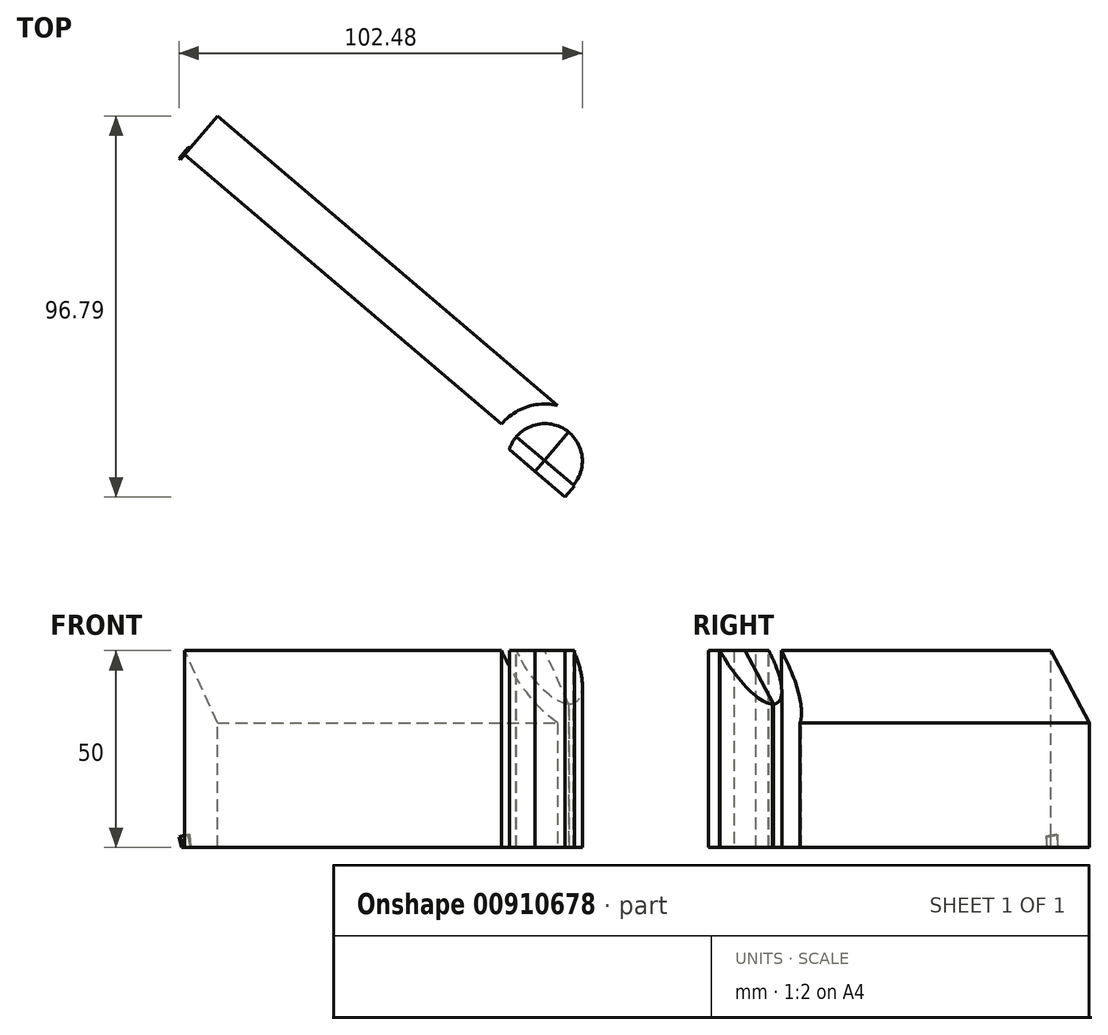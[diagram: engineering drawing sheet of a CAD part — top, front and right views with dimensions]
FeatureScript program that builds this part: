
annotation { "Feature Type Name" : "Feature", "Feature Type Description" : "" }
export const myFeature = defineFeature(function(context is Context, id is Id, definition is map)
    precondition{}
    {
        {
            var Q0;
            Q0=qCreatedBy(makeId("Top.planeOp"),FACE);
            var sketch = newSketch(context, id + "F0", { "sketchPlane" : qUnion([Q0])});
            skArc(sketch, "E0", {"start": v(-9.5, 0) * mm, "mid": v(4.39, 8.43) * mm, "end": v(5.45, -7.78) * mm});
            skLineSegment(sketch, "E1", {"start": v(0, 0) * mm, "end": v(-9.5, 0) * mm, "construction": true});
            skLineSegment(sketch, "E2", {"start": v(0, 0) * mm, "end": v(5.45, -7.78) * mm, "construction": true});
            skArc(sketch, "E3", {"start": v(-14.5, 0) * mm, "mid": v(6.7, 12.86) * mm, "end": v(8.32, -11.88) * mm});
            skLineSegment(sketch, "E4", {"start": v(-14.5, 0) * mm, "end": v(-9.5, 0) * mm});
            skLineSegment(sketch, "E5", {"start": v(5.45, -7.78) * mm, "end": v(8.32, -11.88) * mm});
            skCircle(sketch, "E6", {"center": v(0, 0) * mm, "radius": 9.5 * mm, "construction": true});
            skCircle(sketch, "E7", {"center": v(0, 0) * mm, "radius": 14.5 * mm, "construction": true});
            skSolve(sketch);
        }
        {
            var Q0;
            Q0 = qSketchRegion(id + "F0", true);
            extrude(context, id + "F1", {"entities" : qUnion([Q0]), "depth" : 50 * mm, "offsetDistance" : 25.4 * mm});
        }
        {
            var Q0;
            Q0=makeQuery(id+"F1.opExtrude","CAP_FACE",FACE,{"disambiguationData":[OSD([sQuery(id+"F0.wireOp",EDGE,"E0"),sQuery(id+"F0.wireOp",EDGE,"E3"),sQuery(id+"F0.wireOp",EDGE,"E4"),sQuery(id+"F0.wireOp",EDGE,"E5")])],"isStart":true});
            var sketch = newSketch(context, id + "F2", { "sketchPlane" : qUnion([Q0])});
            skLineSegment(sketch, "E8", {"start": v(-6.15, 7.24) * mm, "end": v(0, 0) * mm, "construction": true});
            skSolve(sketch);
        }
        {
            var Q0;
            Q0=sQuery(id+"F2.wireOp",EDGE,"E8");
            cPlane(context, id + "F3", {"entities" : qUnion([Q0]), "cplaneType" : CPlaneType.LINE_ANGLE, "offset" : 25.4 * mm, "angle" : 90 * degree, "width" : 152.4 * mm, "height" : 152.4 * mm});
        }
        {
            var Q0;
            Q0=qCreatedBy(id+"F3.planeOp",FACE);
            cPlane(context, id + "F4", {"entities" : qUnion([Q0]), "cplaneType" : CPlaneType.OFFSET, "offset" : 2.9 / 20 * mm, "width" : 152.4 * mm, "height" : 152.4 * mm});
        }
        {
            var Q0;
            Q0=makeQuery(id+"F1.opExtrude","SWEPT_EDGE",EDGE,{"disambiguationData":[OSD([sQuery(id+"F0.wireOp",EDGE,"E0"),sQuery(id+"F0.wireOp",EDGE,"E5")])]});
            var Q1;
            Q1=makeQuery(id+"F1.opExtrude","SWEPT_EDGE",EDGE,{"disambiguationData":[OSD([sQuery(id+"F0.wireOp",EDGE,"E0"),sQuery(id+"F0.wireOp",EDGE,"E4")])]});
            fillet(context, id + "F5", {"entities" : qUnion([Q0, Q1]), "radius" : 5 * mm, "tangentPropagation" : true, "allowEdgeOverflow" : false});
        }
        {
            var Q0;
            Q0=qCreatedBy(id+"F4.planeOp",FACE);
            var sketch = newSketch(context, id + "F6", { "sketchPlane" : qUnion([Q0])});
            skLineSegment(sketch, "E9", {"start": v(0, 0) * mm, "end": v(0, 50) * mm, "construction": true});
            skLineSegment(sketch, "E10", {"start": v(35.01, 0) * mm, "end": v(0, 0) * mm, "construction": true});
            skLineSegment(sketch, "E11", {"start": v(35.01, 0) * mm, "end": v(25.18, -6.88) * mm, "construction": true});
            skLineSegment(sketch, "E12", {"start": v(0, 50) * mm, "end": v(-9.83, 43.12) * mm, "construction": true});
            skLineSegment(sketch, "E13", {"start": v(-9.83, 43.12) * mm, "end": v(25.18, -6.88) * mm, "construction": true});
            skLineSegment(sketch, "E14", {"start": v(0, 50) * mm, "end": v(-3.66, 50) * mm, "construction": true});
            skLineSegment(sketch, "E15", {"start": v(-3.66, 50) * mm, "end": v(-3.66, 47.44) * mm, "construction": true});
            skLineSegment(sketch, "E16", {"start": v(-3.66, 47.44) * mm, "end": v(-3.66, 34.3) * mm, "construction": true});
            skLineSegment(sketch, "E17", {"start": v(-3.66, 50) * mm, "end": v(12.84, 50) * mm, "construction": true});
            skLineSegment(sketch, "E18", {"start": v(12.84, 50) * mm, "end": v(12.84, 0) * mm, "construction": true});
            skLineSegment(sketch, "E19", {"start": v(0, 50) * mm, "end": v(-3.66, 50) * mm});
            skLineSegment(sketch, "E20", {"start": v(-3.66, 50) * mm, "end": v(-3.66, 34.3) * mm});
            skLineSegment(sketch, "E21", {"start": v(-3.66, 34.3) * mm, "end": v(12.84, 10.74) * mm});
            skLineSegment(sketch, "E22", {"start": v(12.84, 10.74) * mm, "end": v(12.84, 0) * mm});
            skLineSegment(sketch, "E23", {"start": v(-3.66, 0) * mm, "end": v(12.84, 0) * mm});
            skLineSegment(sketch, "E24", {"start": v(12.84, 10.74) * mm, "end": v(12.84, 31.66) * mm});
            skLineSegment(sketch, "E25", {"start": v(12.84, 31.66) * mm, "end": v(0, 50) * mm});
            skLineSegment(sketch, "E26", {"start": v(0, 50) * mm, "end": v(35.01, 0) * mm, "construction": true});
            skLineSegment(sketch, "E27", {"start": v(-3.66, 50) * mm, "end": v(-3.66, 0) * mm});
            skSolve(sketch);
        }
        {
            var Q0;
            Q0 = qSketchRegion(id + "F6", true);
            extrude(context, id + "F7", {"entities" : qUnion([Q0]), "operationType" : NewBodyOperationType.ADD, "depth" : 120 * mm, "offsetDistance" : 25.4 * mm});
        }
        {
            var Q0;
            Q0=makeQuery(id+"F7.opExtrude","CAP_FACE",FACE,{"disambiguationData":[OSD([sQuery(id+"F6.wireOp",EDGE,"E19"),sQuery(id+"F6.wireOp",EDGE,"E22"),sQuery(id+"F6.wireOp",EDGE,"E23"),sQuery(id+"F6.wireOp",EDGE,"E24"),sQuery(id+"F6.wireOp",EDGE,"E25"),sQuery(id+"F6.wireOp",EDGE,"E27")])],"isStart":true});
            extrude(context, id + "F8", {"entities" : qUnion([Q0]), "operationType" : NewBodyOperationType.REMOVE, "depth" : 10 * mm, "offsetDistance" : 25.4 * mm});
        }
        {
            var Q0;
            Q0=makeQuery(id+"F7.opExtrude","CAP_FACE",FACE,{"disambiguationData":[OSD([sQuery(id+"F6.wireOp",EDGE,"E19"),sQuery(id+"F6.wireOp",EDGE,"E22"),sQuery(id+"F6.wireOp",EDGE,"E23"),sQuery(id+"F6.wireOp",EDGE,"E24"),sQuery(id+"F6.wireOp",EDGE,"E25"),sQuery(id+"F6.wireOp",EDGE,"E27")])],"isStart":true});
            extrude(context, id + "F9", {"entities" : qUnion([Q0]), "depth" : 10 * mm, "offsetDistance" : 25.4 * mm});
        }
        {
            var Q0;
            Q0=makeQuery(id+"F1.opExtrude","CAP_FACE",FACE,{"disambiguationData":[OSD([sQuery(id+"F0.wireOp",EDGE,"E0"),sQuery(id+"F0.wireOp",EDGE,"E3"),sQuery(id+"F0.wireOp",EDGE,"E4"),sQuery(id+"F0.wireOp",EDGE,"E5")])],"isStart":false});
            var sketch = newSketch(context, id + "F10", { "sketchPlane" : qUnion([Q0])});
            skCircle(sketch, "E28", {"center": v(0, 0) * mm, "radius": 9.5 * mm});
            skSolve(sketch);
        }
        {
            var Q0;
            {var subQ0=sQuery(id+"F10.wireOp",EDGE,"E28");Q0=makeQuery(id+"F10.imprint","IMPRINT",FACE,{"disambiguationData":[TD([[makeQuery(id+"F10.imprint","IMPRINT",EDGE,{"disambiguationData":[OD(0.0)],"derivedFrom":subQ0}),-1.0]])]});}
            extrude(context, id + "F11", {"entities" : qUnion([Q0]), "operationType" : NewBodyOperationType.REMOVE, "oppositeDirection" : true, "depth" : 50 * mm, "offsetDistance" : 25.4 * mm});
        }
        {
            var Q0;
            Q0=makeQuery(id+"F7.opExtrude","CAP_EDGE",EDGE,{"disambiguationData":[OSD([sQuery(id+"F6.wireOp",EDGE,"E23")])],"isStart":false});
            cPlane(context, id + "F12", {"entities" : qUnion([Q0]), "cplaneType" : CPlaneType.LINE_ANGLE, "offset" : 25.4 * mm, "angle" : 90 * degree, "width" : 152.4 * mm, "height" : 152.4 * mm});
        }
        {
            var Q0;
            Q0=makeQuery(id+"F1.opExtrude","SWEPT_BODY",BODY,{"disambiguationData":[OSD([sQuery(id+"F0.wireOp",EDGE,"E0"),sQuery(id+"F0.wireOp",EDGE,"E3"),sQuery(id+"F0.wireOp",EDGE,"E4"),sQuery(id+"F0.wireOp",EDGE,"E5")])]});
            var Q1;
            Q1=makeQuery(id+"F7.opExtrude","SWEPT_BODY",BODY,{"disambiguationData":[OSD([sQuery(id+"F6.wireOp",EDGE,"E19"),sQuery(id+"F6.wireOp",EDGE,"E22"),sQuery(id+"F6.wireOp",EDGE,"E23"),sQuery(id+"F6.wireOp",EDGE,"E24"),sQuery(id+"F6.wireOp",EDGE,"E25"),sQuery(id+"F6.wireOp",EDGE,"E27")])]});
            var Q2;
            Q2=makeQuery(id+"F9.opExtrude","SWEPT_BODY",BODY,{"disambiguationData":[OSD([sQuery(id+"F6.wireOp",EDGE,"E19"),sQuery(id+"F6.wireOp",EDGE,"E22"),sQuery(id+"F6.wireOp",EDGE,"E23"),sQuery(id+"F6.wireOp",EDGE,"E24"),sQuery(id+"F6.wireOp",EDGE,"E25"),sQuery(id+"F6.wireOp",EDGE,"E27")])]});
            var Q3;
            Q3=qCreatedBy(id+"F12.planeOp",FACE);
            mirror(context, id + "F13", {"entities" : qUnion([Q0, Q1, Q2]), "mirrorPlane" : qUnion([Q3])});
        }
        {
            var Q0;
            Q0=makeQuery(id+"F9.opExtrude","SWEPT_BODY",BODY,{"disambiguationData":[OSD([sQuery(id+"F6.wireOp",EDGE,"E19"),sQuery(id+"F6.wireOp",EDGE,"E22"),sQuery(id+"F6.wireOp",EDGE,"E23"),sQuery(id+"F6.wireOp",EDGE,"E24"),sQuery(id+"F6.wireOp",EDGE,"E25"),sQuery(id+"F6.wireOp",EDGE,"E27")])]});
            var Q1;
            Q1=makeQuery(id+"F1.opExtrude","SWEPT_BODY",BODY,{"disambiguationData":[OSD([sQuery(id+"F0.wireOp",EDGE,"E0"),sQuery(id+"F0.wireOp",EDGE,"E3"),sQuery(id+"F0.wireOp",EDGE,"E4"),sQuery(id+"F0.wireOp",EDGE,"E5")])]});
            var Q2;
            Q2=makeQuery(id+"F7.opExtrude","SWEPT_BODY",BODY,{"disambiguationData":[OSD([sQuery(id+"F6.wireOp",EDGE,"E19"),sQuery(id+"F6.wireOp",EDGE,"E22"),sQuery(id+"F6.wireOp",EDGE,"E23"),sQuery(id+"F6.wireOp",EDGE,"E24"),sQuery(id+"F6.wireOp",EDGE,"E25"),sQuery(id+"F6.wireOp",EDGE,"E27")])]});
            deleteBodies(context, id + "F14", {"entities" : qUnion([Q0, Q1, Q2])});
        }
        {
            var Q0;
            Q0=makeQuery(id+"F13.opPattern","COPY",BODY,{"derivedFrom":makeQuery(id+"F7.opExtrude","SWEPT_BODY",BODY,{"disambiguationData":[OSD([sQuery(id+"F6.wireOp",EDGE,"E19"),sQuery(id+"F6.wireOp",EDGE,"E22"),sQuery(id+"F6.wireOp",EDGE,"E23"),sQuery(id+"F6.wireOp",EDGE,"E24"),sQuery(id+"F6.wireOp",EDGE,"E25"),sQuery(id+"F6.wireOp",EDGE,"E27")])]}),"instanceName":"1"});
            var Q1;
            Q1=makeQuery(id+"F13.opPattern","COPY",BODY,{"derivedFrom":makeQuery(id+"F1.opExtrude","SWEPT_BODY",BODY,{"disambiguationData":[OSD([sQuery(id+"F0.wireOp",EDGE,"E0"),sQuery(id+"F0.wireOp",EDGE,"E3"),sQuery(id+"F0.wireOp",EDGE,"E4"),sQuery(id+"F0.wireOp",EDGE,"E5")])]}),"instanceName":"1"});
            var Q2;
            Q2=makeQuery(id+"F13.opPattern","COPY",BODY,{"derivedFrom":makeQuery(id+"F9.opExtrude","SWEPT_BODY",BODY,{"disambiguationData":[OSD([sQuery(id+"F6.wireOp",EDGE,"E19"),sQuery(id+"F6.wireOp",EDGE,"E22"),sQuery(id+"F6.wireOp",EDGE,"E23"),sQuery(id+"F6.wireOp",EDGE,"E24"),sQuery(id+"F6.wireOp",EDGE,"E25"),sQuery(id+"F6.wireOp",EDGE,"E27")])]}),"instanceName":"1"});
            var Q3;
            Q3=makeQuery(id+"F13.opPattern","COPY",EDGE,{"derivedFrom":makeQuery(id+"F7.opExtrude","SWEPT_EDGE",EDGE,{"disambiguationData":[OSD([sQuery(id+"F6.wireOp",EDGE,"E22"),sQuery(id+"F6.wireOp",EDGE,"E23")])]}),"instanceName":"1"});
            transform(context, id + "F15", {"entities" : qUnion([Q0, Q1, Q2]), "transformType" : TransformType.TRANSLATION_3D, "dx" : -419.1 * mm, "dy" : 320.04 * mm, "dz" : 0 * mm, "makeCopy" : false});
        }
        {
            var Q0;
            Q0=makeQuery(id+"F13.opPattern","COPY",EDGE,{"derivedFrom":makeQuery(id+"F7.opExtrude","CAP_EDGE",EDGE,{"disambiguationData":[OSD([sQuery(id+"F6.wireOp",EDGE,"E23")])],"isStart":false}),"instanceName":"1"});
            cPlane(context, id + "F16", {"entities" : qUnion([Q0]), "cplaneType" : CPlaneType.LINE_ANGLE, "offset" : 25.4 * mm, "angle" : 80 * degree, "width" : 152.4 * mm, "height" : 152.4 * mm});
        }
        {
            var Q0;
            Q0=qCreatedBy(id+"F16.planeOp",FACE);
            var sketch = newSketch(context, id + "F17", { "sketchPlane" : qUnion([Q0])});
            skLineSegment(sketch, "E29.bottom", {"start": v(-18.42, 30.83) * mm, "end": v(-14.79, 30.83) * mm});
            skLineSegment(sketch, "E29.top", {"start": v(-18.42, 76.79) * mm, "end": v(-14.79, 76.79) * mm});
            skLineSegment(sketch, "E29.left", {"start": v(-18.42, 30.83) * mm, "end": v(-18.42, 76.79) * mm});
            skLineSegment(sketch, "E29.right", {"start": v(-14.79, 30.83) * mm, "end": v(-14.79, 76.79) * mm});
            skSolve(sketch);
        }
        {
            var Q0;
            Q0=makeQuery(id+"F17.imprint","IMPRINT",FACE,{"disambiguationData":[TD([[makeQuery(id+"F17.imprint","IMPRINT",EDGE,{"derivedFrom":sQuery(id+"F17.wireOp",EDGE,"E29.bottom")}),1.0]])]});
            var Q1;
            Q1=makeQuery(id+"F13.opPattern","COPY",FACE,{"derivedFrom":makeQuery(id+"F7.opExtrude","CAP_FACE",FACE,{"disambiguationData":[OSD([sQuery(id+"F6.wireOp",EDGE,"E19"),sQuery(id+"F6.wireOp",EDGE,"E22"),sQuery(id+"F6.wireOp",EDGE,"E23"),sQuery(id+"F6.wireOp",EDGE,"E24"),sQuery(id+"F6.wireOp",EDGE,"E25"),sQuery(id+"F6.wireOp",EDGE,"E27")])],"isStart":false}),"instanceName":"1"});
            extrude(context, id + "F18", {"entities" : qUnion([Q0]), "operationType" : NewBodyOperationType.ADD, "endBound" : BoundingType.UP_TO_SURFACE, "depth" : 2.54 * mm, "endBoundEntityFace" : qUnion([Q1]), "offsetDistance" : 25.4 * mm});
        }
    });
